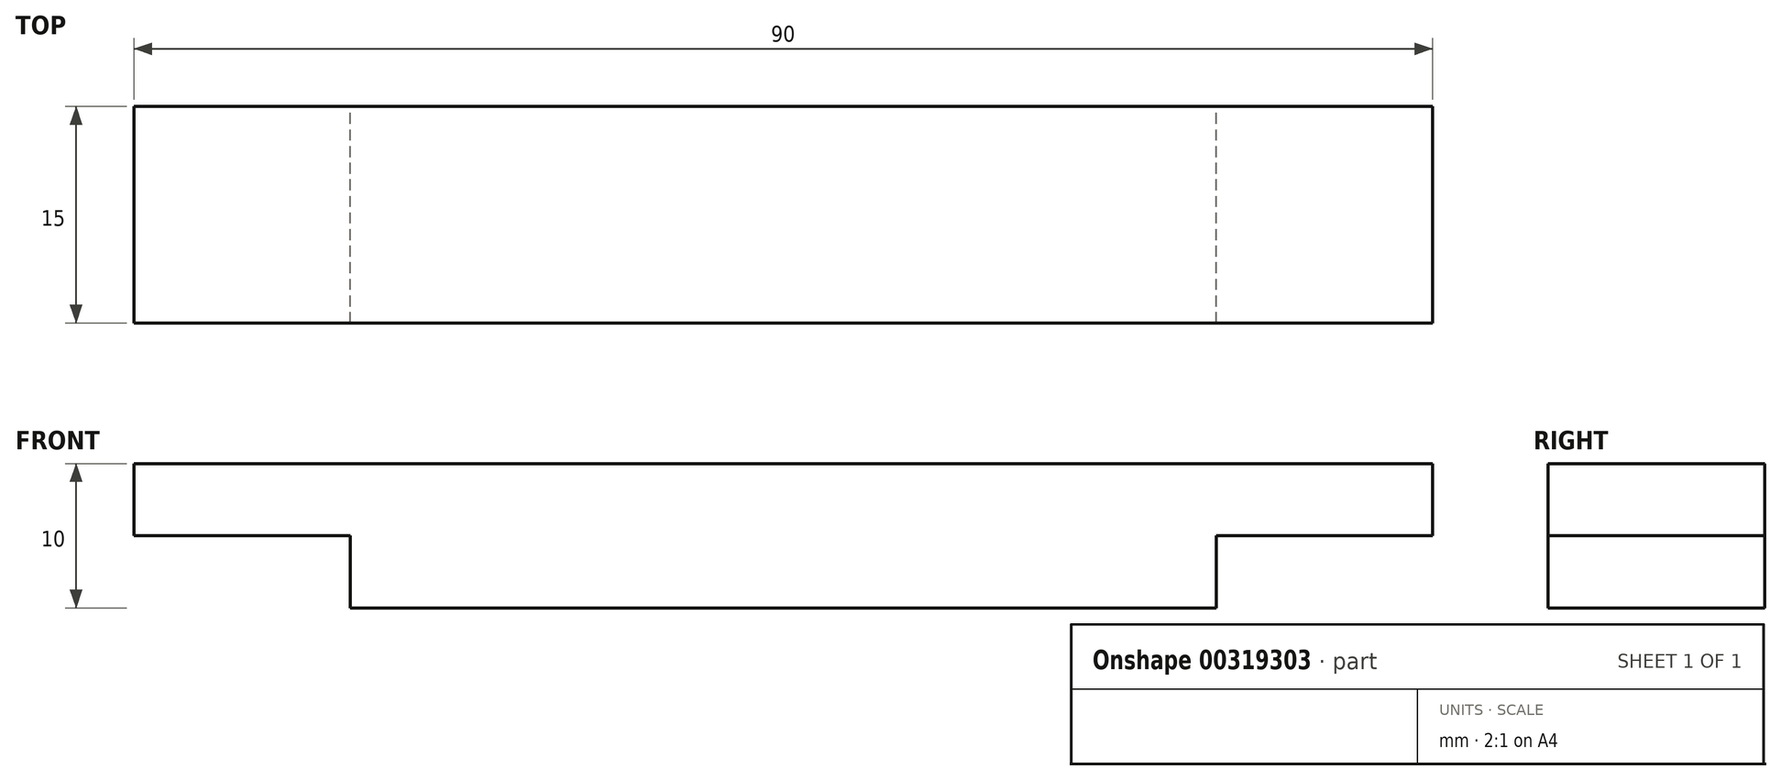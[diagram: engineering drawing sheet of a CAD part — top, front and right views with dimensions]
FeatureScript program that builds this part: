
annotation { "Feature Type Name" : "Feature", "Feature Type Description" : "" }
export const myFeature = defineFeature(function(context is Context, id is Id, definition is map)
    precondition{}
    {
        {
            var Q0;
            Q0=qCreatedBy(makeId("Front.planeOp"),FACE);
            var sketch = newSketch(context, id + "F0", { "sketchPlane" : qUnion([Q0])});
            skLineSegment(sketch, "E0", {"start": v(-35.6, 0) * mm, "end": v(24.4, 0) * mm});
            skLineSegment(sketch, "E1", {"start": v(24.4, 0) * mm, "end": v(24.4, 5) * mm});
            skLineSegment(sketch, "E2", {"start": v(24.4, 5) * mm, "end": v(39.4, 5) * mm});
            skLineSegment(sketch, "E3", {"start": v(39.4, 5) * mm, "end": v(39.4, 10) * mm});
            skLineSegment(sketch, "E4", {"start": v(39.4, 10) * mm, "end": v(-50.6, 10) * mm});
            skLineSegment(sketch, "E5", {"start": v(-50.6, 10) * mm, "end": v(-50.6, 5) * mm});
            skLineSegment(sketch, "E6", {"start": v(-50.6, 5) * mm, "end": v(-35.6, 5) * mm});
            skLineSegment(sketch, "E7", {"start": v(-35.6, 5) * mm, "end": v(-35.6, 0) * mm});
            skSolve(sketch);
        }
        {
            var Q0;
            Q0 = qSketchRegion(id + "F0", true);
            extrude(context, id + "F1", {"entities" : qUnion([Q0]), "depth" : 15 * mm});
        }
    });
